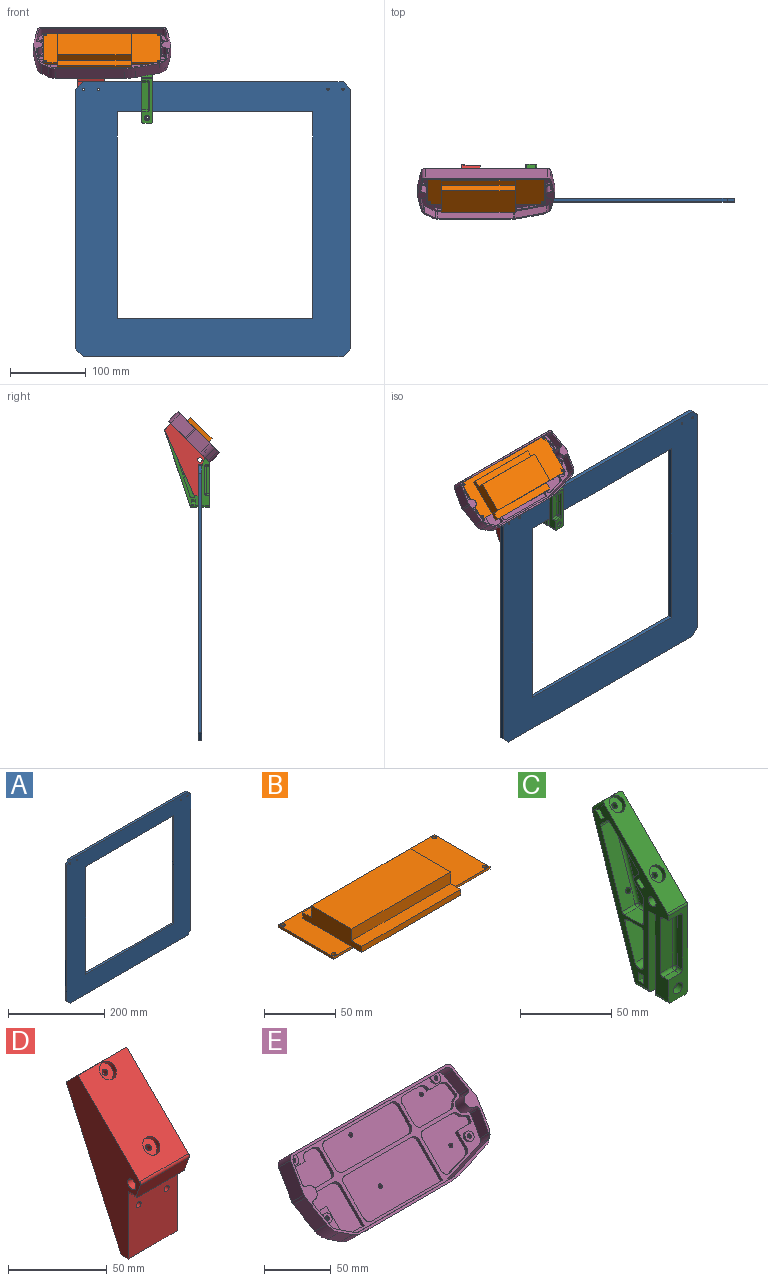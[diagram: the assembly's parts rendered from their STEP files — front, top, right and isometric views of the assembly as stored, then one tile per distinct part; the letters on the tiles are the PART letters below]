
ASSEMBLY  parts=5 mates=4
PART A: 18 faces, bbox 364x5x364 mm
  f0: plane 344x5mm, normal (-1,0,0), area 1720mm2, adj f12,f13,f16,f17
  f1: plane 344x5mm, normal (0,0,-1), area 1720mm2, adj f12,f13,f15,f16
  f2: plane 344x5mm, normal (1,0,0), area 1720mm2, adj f12,f13,f14,f15
  f3: plane 259x5mm, normal (0,0,1), area 1295mm2, adj f4,f6,f12,f13
  f4: plane 274x5mm, normal (1,0,0), area 1370mm2, adj f3,f5,f12,f13
  f5: plane 259x5mm, normal (0,0,-1), area 1295mm2, adj f4,f6,f12,f13
  f6: plane 274x5mm, normal (-1,0,0), area 1370mm2, adj f3,f5,f12,f13
  f7: cylinder r=1.5mm len=5mm, axis (0,1,0), area 47.1mm2, adj f12,f13
  f8: cylinder r=1.5mm len=5mm, axis (0,1,0), area 47.1mm2, adj f12,f13
  f9: cylinder r=1.5mm len=5mm, axis (0,1,0), area 47.1mm2, adj f12,f13
  f10: cylinder r=1.5mm len=5mm, axis (0,1,0), area 47.1mm2, adj f12,f13
  f11: plane 344x5mm, normal (0,0,1), area 1720mm2, adj f12,f13,f14,f17
  f12: plane 364x364mm, normal (0,-1,0), area 61301.7mm2, adj f0,f1,f2,f3,f4,f5,f6,f7
  f13: plane 364x364mm, normal (0,1,0), area 61301.7mm2, adj f0,f1,f2,f3,f4,f5,f6,f7
  f14: plane 10x10mm, normal (0.71,0,0.71), area 70.7mm2, adj f2,f11,f12,f13
  f15: plane 10x10mm, normal (0.71,0,-0.71), area 70.7mm2, adj f1,f2,f12,f13
  f16: plane 10x10mm, normal (-0.71,0,-0.71), area 70.7mm2, adj f0,f1,f12,f13
  f17: plane 10x10mm, normal (-0.71,0,0.71), area 70.7mm2, adj f0,f11,f12,f13
PART B: 20 faces, bbox 155x65x17 mm
  f0: plane 98x8.51mm, normal (0,0,1), area 834.2mm2, adj f12,f13,f15,f17
  f1: plane 155x55mm, normal (0,0,1), area 3732.3mm2, adj f2,f3,f4,f5,f6,f7,f8,f9
  f2: plane 155x2mm, normal (0,1,0), area 310mm2, adj f1,f3,f9,f10
  f3: plane 55x2mm, normal (-1,0,0), area 110mm2, adj f1,f2,f4,f10
  f4: plane 155x2mm, normal (0,-1,0), area 310mm2, adj f1,f3,f9,f10,f11
  f5: cylinder r=1.75mm len=3.5mm, axis (0,0,-1), area 22mm2, adj f1,f10
  f6: cylinder r=1.75mm len=3.5mm, axis (0,0,-1), area 22mm2, adj f1,f10
  f7: cylinder r=1.75mm len=3.5mm, axis (0,0,-1), area 22mm2, adj f1,f10
  f8: cylinder r=1.75mm len=3.5mm, axis (0,0,-1), area 22mm2, adj f1,f10
  f9: plane 55x2mm, normal (1,0,0), area 110mm2, adj f1,f2,f4,f10
  f10: plane 155x55mm, normal (0,0,-1), area 8486.5mm2, adj f2,f3,f4,f5,f6,f7,f8,f9
  f11: plane 98x10mm, normal (0,0,-1), area 980mm2, adj f4,f13,f14,f15
  f12: plane 98x5mm, normal (0,1,0), area 490mm2, adj f0,f1,f13,f15
  f13: plane 58.51x15mm, normal (-1,0,0), area 692.6mm2, adj f0,f1,f11,f12,f14,f16,f17,f18
  f14: plane 98x5mm, normal (0,-1,0), area 490mm2, adj f11,f13,f15,f16
  f15: plane 58.51x15mm, normal (1,0,0), area 692.6mm2, adj f0,f1,f11,f12,f14,f16,f17,f18
  f16: plane 98x10mm, normal (0,0,1), area 980mm2, adj f13,f14,f15,f18
  f17: plane 98x10mm, normal (0,1,0), area 980mm2, adj f0,f13,f15,f19
  f18: plane 98x10mm, normal (0,-1,0), area 980mm2, adj f13,f15,f16,f19
  f19: plane 98x40mm, normal (0,0,1), area 3920mm2, adj f13,f15,f17,f18
PART C: 98 faces, bbox 15.4x60.5x111.3 mm
  f0: cylinder r=1.75mm len=4mm, axis (0,-1,0), area 44mm2, adj f8,f79
  f1: cylinder r=1.7mm len=3.82mm, axis (0,-0.71,0.71), area 21.4mm2, adj f40,f50
  f2: cylinder r=1.7mm len=6.77mm, axis (0,-0.71,0.71), area 47.7mm2, adj f10,f58
  f3: plane 107.5x58.69mm, normal (-1,0,0), area 1499mm2, adj f5,f6,f7,f8,f10,f12,f25,f29
  f4: cylinder r=1.7mm len=6.35mm, axis (0,-0.71,0.71), area 50.6mm2, adj f10,f46
  f5: plane 59.17x15mm, normal (0,-1,0), area 409.1mm2, adj f3,f13,f14,f18,f25,f28,f31,f33
  f6: plane 55x15mm, normal (0,1,0), area 813.7mm2, adj f3,f7,f13,f14,f16,f28,f31
  f7: plane 15x5mm, normal (0,0,-1), area 75mm2, adj f3,f6,f8,f14
  f8: plane 55x15mm, normal (0,-1,0), area 813.7mm2, adj f0,f3,f7,f9,f14,f27,f30
  f9: plane 11x10mm, normal (0,0,-1), area 110mm2, adj f8,f10,f27,f30
  f10: plane 102.78x34.75mm, normal (0,0.95,-0.32), area 1586.6mm2, adj f2,f3,f4,f9,f11,f14,f15,f26
  f11: plane 11x8.49mm, normal (0,0.71,0.71), area 132mm2, adj f10,f12,f26,f29
  f12: plane 50.33x50.33mm, normal (0,-0.71,0.71), area 908.8mm2, adj f3,f11,f14,f19,f21,f25,f26,f29
  f13: plane 11x10mm, normal (0,0,-1), area 110mm2, adj f5,f6,f28,f31
  f14: plane 107.5x58.69mm, normal (1,0,0), area 3125.2mm2, adj f5,f6,f7,f8,f10,f12,f25,f26
  f15: cylinder r=1.75mm len=4.95mm, axis (0,-1,0), area 47.8mm2, adj f10,f77
  f16: cylinder r=1.75mm len=6mm, axis (0,-1,0), area 66mm2, adj f6,f17
  f17: plane 7x7mm, normal (0,-1,0), area 28.9mm2, adj f16,f18
  f18: cylinder r=3.5mm len=7mm, axis (0,-1,0), area 88mm2, adj f5,f17
  f19: cylinder r=5mm len=10mm, axis (0,-0.71,0.71), area 94.2mm2, adj f12,f20
  f20: plane 10x7.07mm, normal (0,-0.71,0.71), area 69.5mm2, adj f19,f24
  f21: cylinder r=5mm len=10mm, axis (0,-0.71,0.71), area 94.2mm2, adj f12,f22
  f22: plane 10x7.07mm, normal (0,-0.71,0.71), area 69.5mm2, adj f21,f23
  f23: cylinder r=1.7mm len=4.88mm, axis (0,-0.71,0.71), area 37.4mm2, adj f22,f47
  f24: cylinder r=1.7mm len=4.88mm, axis (0,-0.71,0.71), area 37.4mm2, adj f20,f41
  f25: cylinder r=2mm len=15mm, axis (1,0,0), area 23.6mm2, adj f3,f5,f12,f14
  f26: cylinder r=2mm len=10.6mm, axis (0,-0.71,0.71), area 38.8mm2, adj f10,f11,f12,f14
  f27: cylinder r=2mm len=10.67mm, axis (0,1,0), area 32.5mm2, adj f8,f9,f10,f14
  f28: cylinder r=2mm len=10mm, axis (0,1,0), area 31.4mm2, adj f5,f6,f13,f14
  f29: cylinder r=2mm len=10.6mm, axis (0,0.71,-0.71), area 38.8mm2, adj f3,f10,f11,f12
  f30: cylinder r=2mm len=10.67mm, axis (0,-1,0), area 32.5mm2, adj f3,f8,f9,f10
  f31: cylinder r=2mm len=10mm, axis (0,-1,0), area 31.4mm2, adj f3,f5,f6,f13
  f32: plane 36x9mm, normal (0,-1,0), area 324mm2, adj f3,f70,f73,f76
  f33: plane 9x4mm, normal (0,0,1), area 36mm2, adj f3,f5,f74,f76
  f34: plane 36x4mm, normal (-1,0,0), area 144mm2, adj f5,f71,f73,f74
  f35: plane 9x4mm, normal (0,0,-1), area 36mm2, adj f3,f5,f70,f71
  f36: plane 9.38x2.48mm, normal (0,0.71,0.71), area 32.8mm2, adj f3,f37,f40,f41
  f37: plane 4.45x4.45mm, normal (-0.87,0.35,0.35), area 11.3mm2, adj f36,f38,f40,f41
  f38: plane 4.45x4.45mm, normal (-0.87,-0.35,-0.35), area 11.3mm2, adj f37,f39,f40,f41
  f39: plane 9.38x2.48mm, normal (0,-0.71,-0.71), area 32.8mm2, adj f3,f38,f40,f41
  f40: plane 11x3.96mm, normal (0,-0.71,0.71), area 48mm2, adj f1,f3,f36,f37,f38,f39
  f41: plane 11x3.96mm, normal (0,0.71,-0.71), area 48mm2, adj f3,f24,f36,f37,f38,f39
  f42: plane 9.38x2.48mm, normal (0,0.71,0.71), area 32.8mm2, adj f3,f43,f46,f47
  f43: plane 4.45x4.45mm, normal (-0.87,0.35,0.35), area 11.3mm2, adj f42,f44,f46,f47
  f44: plane 4.45x4.45mm, normal (-0.87,-0.35,-0.35), area 11.3mm2, adj f43,f45,f46,f47
  f45: plane 9.38x2.48mm, normal (0,-0.71,-0.71), area 32.8mm2, adj f3,f44,f46,f47
  f46: plane 11x3.96mm, normal (0,-0.71,0.71), area 48mm2, adj f3,f4,f42,f43,f44,f45
  f47: plane 11x3.96mm, normal (0,0.71,-0.71), area 48mm2, adj f3,f23,f42,f43,f44,f45
  f48: plane 52.97x29.29mm, normal (-1,0,0), area 741.1mm2, adj f84,f87,f88,f90,f91,f92,f95,f96
  f49: cylinder r=2mm len=10mm, axis (-1,0,0), area 15.7mm2, adj f3,f50,f60,f94
  f50: plane 10x6.79mm, normal (0,0.71,-0.71), area 86.9mm2, adj f1,f3,f49,f51,f92
  f51: cylinder r=2mm len=10mm, axis (-1,0,0), area 31.4mm2, adj f3,f50,f52,f90
  f52: plane 10x2.83mm, normal (0,0.71,0.71), area 40mm2, adj f3,f51,f53,f88
  f53: cylinder r=2mm len=10mm, axis (-1,0,0), area 31.4mm2, adj f3,f52,f54,f86
  f54: plane 21.5x21.5mm, normal (0,0.71,-0.71), area 304mm2, adj f3,f53,f55,f84
  f55: cylinder r=2mm len=10mm, axis (-1,0,0), area 31.4mm2, adj f3,f54,f56,f85
  f56: plane 10x3.83mm, normal (0,-0.71,-0.71), area 54.1mm2, adj f3,f55,f57,f87
  f57: cylinder r=2mm len=10mm, axis (-1,0,0), area 22.2mm2, adj f3,f56,f58,f89
  f58: plane 49.14x16.5mm, normal (0,-0.95,0.32), area 508.3mm2, adj f2,f3,f57,f59,f91
  f59: cylinder r=2mm len=10mm, axis (-1,0,0), area 24.9mm2, adj f3,f58,f61,f93
  f60: plane 16.2x10mm, normal (0,1,0), area 162mm2, adj f3,f49,f62,f96
  f61: plane 12.78x10mm, normal (0,0,1), area 127.8mm2, adj f3,f59,f62,f95
  f62: cylinder r=2mm len=10mm, axis (-1,0,0), area 31.4mm2, adj f3,f60,f61,f97
  f63: plane 28.39x14.77mm, normal (-1,0,0), area 299.6mm2, adj f64,f65,f66,f67,f68,f69
  f64: cylinder r=2mm len=12mm, axis (-1,0,0), area 37.7mm2, adj f3,f63,f65,f69
  f65: plane 12x10.77mm, normal (0,0,-1), area 129.2mm2, adj f3,f63,f64,f66
  f66: cylinder r=2mm len=12mm, axis (-1,0,0), area 45.5mm2, adj f3,f63,f65,f67
  f67: plane 23.36x12mm, normal (0,-0.95,0.32), area 295.7mm2, adj f3,f63,f66,f68
  f68: cylinder r=3.5mm len=12mm, axis (-1,0,0), area 118.3mm2, adj f3,f63,f67,f69
  f69: plane 22.89x12mm, normal (0,1,0), area 274.6mm2, adj f3,f63,f64,f68
  f70: cylinder r=2mm len=9mm, axis (1,0,0), area 28.3mm2, adj f3,f32,f35,f72
  f71: cylinder r=2mm len=4mm, axis (0,1,0), area 12.6mm2, adj f5,f34,f35,f72
  f72: sphere r=2mm, area 6.3mm2, adj f70,f71,f73
  f73: cylinder r=2mm len=36mm, axis (0,0,-1), area 113.1mm2, adj f32,f34,f72,f75
  f74: cylinder r=2mm len=4mm, axis (0,-1,0), area 12.6mm2, adj f5,f33,f34,f75
  f75: sphere r=2mm, area 6.3mm2, adj f73,f74,f76
  f76: cylinder r=2mm len=9mm, axis (-1,0,0), area 28.3mm2, adj f3,f32,f33,f75
  f77: plane 13.8x5.6mm, normal (0,-1,0), area 63.1mm2, adj f3,f15,f78,f80,f81,f82
  f78: plane 12.18x4mm, normal (0,0,1), area 48.7mm2, adj f3,f77,f79,f82
  f79: plane 13.8x5.6mm, normal (0,1,0), area 63.1mm2, adj f0,f3,f78,f80,f81,f82
  f80: plane 12.18x4mm, normal (0,0,-1), area 48.7mm2, adj f3,f77,f79,f81
  f81: plane 4x2.8mm, normal (-0.87,0,-0.5), area 12.9mm2, adj f77,f79,f80,f82
  f82: plane 4x2.8mm, normal (-0.87,0,0.5), area 12.9mm2, adj f77,f78,f79,f81
  f83: cylinder r=3mm len=15mm, axis (1,0,0), area 282.7mm2, adj f3,f14
  f84: cylinder r=2mm len=22.91mm, axis (0,-0.71,-0.71), area 95.5mm2, adj f48,f54,f85,f86
  f85: sphere r=2mm, area 6.3mm2, adj f55,f84,f87
  f86: sphere r=2mm, area 6.3mm2, adj f53,f84,f88
  f87: cylinder r=2mm len=5.24mm, axis (0,-0.71,0.71), area 17mm2, adj f48,f56,f85,f89
  f88: cylinder r=2mm len=4.24mm, axis (0,0.71,-0.71), area 12.6mm2, adj f48,f52,f86,f90
  f89: sphere r=2mm, area 4.4mm2, adj f57,f87,f91
  f90: torus R=4mm, axis (1,0,0), area 13.5mm2, adj f48,f51,f88,f92
  f91: cylinder r=2mm len=49.78mm, axis (0,0.32,0.95), area 162.9mm2, adj f48,f58,f89,f93
  f92: cylinder r=2mm len=8.2mm, axis (0,-0.71,-0.71), area 30.2mm2, adj f48,f50,f90,f94
  f93: sphere r=2mm, area 5mm2, adj f59,f91,f95
  f94: sphere r=2mm, area 3.1mm2, adj f49,f92,f96
  f95: cylinder r=2mm len=12.78mm, axis (0,1,0), area 40.2mm2, adj f48,f61,f93,f97
  f96: cylinder r=2mm len=16.2mm, axis (0,0,-1), area 50.9mm2, adj f48,f60,f94,f97
  f97: sphere r=2mm, area 6.3mm2, adj f62,f95,f96
PART D: 81 faces, bbox 35.1x53.1x96 mm
  f0: plane 38.53x30.5mm, normal (0,1,0), area 395mm2, adj f2,f7,f8,f10,f11,f41,f46,f48
  f1: plane 31.13x31.13mm, normal (0,0.71,-0.71), area 409mm2, adj f2,f3,f4,f9,f42,f43,f44,f54
  f2: cylinder r=20mm len=20.5mm, axis (1,0,0), area 182.7mm2, adj f0,f1,f3,f12,f39,f41,f55,f71
  f3: plane 13.19x11.62mm, normal (1,0,0), area 58.5mm2, adj f1,f2,f5,f26,f29,f30,f39,f42
  f4: plane 16.35x14.35mm, normal (1,0,0), area 84.7mm2, adj f1,f6,f15,f31,f34,f35,f38,f43
  f5: plane 9.38x2.48mm, normal (0,-0.71,-0.71), area 32.8mm2, adj f3,f27,f29,f30
  f6: plane 9.38x2.48mm, normal (0,-0.71,-0.71), area 32.8mm2, adj f4,f32,f34,f35
  f7: plane 86.23x38.89mm, normal (0,0.91,-0.41), area 312.6mm2, adj f0,f8,f14,f19,f36,f51,f54,f56
  f8: plane 95.91x46.72mm, normal (1,0,0), area 436mm2, adj f0,f7,f13,f14,f15,f16,f17,f18
  f9: cylinder r=1.7mm len=3.82mm, axis (0,-0.71,0.71), area 21.4mm2, adj f1,f34
  f10: cylinder r=1.75mm len=6mm, axis (0,-1,0), area 66mm2, adj f0,f13
  f11: cylinder r=1.75mm len=6mm, axis (0,-1,0), area 66mm2, adj f0,f13
  f12: cylinder r=1.7mm len=4.3mm, axis (0,-0.71,0.71), area 25mm2, adj f2,f29
  f13: plane 42x35mm, normal (0,-1,0), area 1381.6mm2, adj f8,f10,f11,f14,f18,f19,f79
  f14: plane 35x5mm, normal (0,0,-1), area 175mm2, adj f7,f8,f13,f19
  f15: plane 35x7.51mm, normal (0,0.71,0.71), area 281.9mm2, adj f4,f8,f16,f19,f38,f75,f76,f77
  f16: plane 44.01x44.01mm, normal (0,-0.71,0.71), area 2021.5mm2, adj f8,f15,f19,f20,f22,f78
  f17: plane 35x9.8mm, normal (0,-0.94,-0.34), area 364.1mm2, adj f8,f18,f19,f78,f79
  f18: plane 33x5mm, normal (0,0,-1), area 165mm2, adj f8,f13,f17,f79
  f19: plane 95.91x52.69mm, normal (-1,0,0), area 1933.1mm2, adj f7,f13,f14,f15,f16,f17,f75,f78
  f20: cylinder r=5mm len=10mm, axis (0,-0.71,0.71), area 94.2mm2, adj f16,f21
  f21: plane 10x7.07mm, normal (0,-0.71,0.71), area 69.5mm2, adj f20,f25
  f22: cylinder r=5mm len=10mm, axis (0,-0.71,0.71), area 94.2mm2, adj f16,f23
  f23: plane 10x7.07mm, normal (0,-0.71,0.71), area 69.5mm2, adj f22,f24
  f24: cylinder r=1.7mm len=4.88mm, axis (0,-0.71,0.71), area 37.4mm2, adj f23,f35
  f25: cylinder r=1.7mm len=4.88mm, axis (0,-0.71,0.71), area 37.4mm2, adj f21,f30
  f26: plane 9.38x2.48mm, normal (0,0.71,0.71), area 32.8mm2, adj f3,f28,f29,f30
  f27: plane 4.45x4.45mm, normal (0.87,-0.35,-0.35), area 11.3mm2, adj f5,f28,f29,f30
  f28: plane 4.45x4.45mm, normal (0.87,0.35,0.35), area 11.3mm2, adj f26,f27,f29,f30
  f29: plane 11x3.96mm, normal (0,-0.71,0.71), area 48mm2, adj f3,f5,f12,f26,f27,f28
  f30: plane 11x3.96mm, normal (0,0.71,-0.71), area 48mm2, adj f3,f5,f25,f26,f27,f28
  f31: plane 9.38x2.48mm, normal (0,0.71,0.71), area 32.8mm2, adj f4,f33,f34,f35
  f32: plane 4.45x4.45mm, normal (0.87,-0.35,-0.35), area 11.3mm2, adj f6,f33,f34,f35
  f33: plane 4.45x4.45mm, normal (0.87,0.35,0.35), area 11.3mm2, adj f31,f32,f34,f35
  f34: plane 11x3.96mm, normal (0,-0.71,0.71), area 48mm2, adj f4,f6,f9,f31,f32,f33
  f35: plane 11x3.96mm, normal (0,0.71,-0.71), area 48mm2, adj f4,f6,f24,f31,f32,f33
  f36: plane 75.62x34.08mm, normal (1,0,0), area 700.9mm2, adj f7,f54,f55,f56
  f37: plane 8x1.36mm, normal (0,0.71,0.71), area 15.4mm2, adj f8,f53,f57,f60
  f38: plane 36.98x36.98mm, normal (0,0.71,-0.71), area 815mm2, adj f4,f8,f15,f49,f50,f53,f58,f68
  f39: plane 13x0.88mm, normal (0,0,-1), area 11.4mm2, adj f2,f3,f47,f71
  f40: plane 23x10.5mm, normal (0,1,0), area 194mm2, adj f8,f47,f48,f57,f62,f73
  f41: plane 11.06x2.07mm, normal (1,0,0), area 12mm2, adj f0,f2,f71,f72,f73,f74
  f42: plane 13x3.54mm, normal (0,0.71,0.71), area 65mm2, adj f1,f3,f50,f66
  f43: plane 13x3.54mm, normal (0,-0.71,-0.71), area 65mm2, adj f1,f4,f49,f70
  f44: plane 24.2x24.2mm, normal (1,0,0), area 197.1mm2, adj f1,f66,f67,f68,f69,f70
  f45: plane 23x16.28mm, normal (0,1,0), area 374.5mm2, adj f8,f51,f52,f64
  f46: plane 19.75x1mm, normal (1,0,0), area 18.7mm2, adj f0,f63,f64,f65
  f47: cylinder r=4mm len=15mm, axis (1,0,0), area 84.9mm2, adj f3,f39,f40,f61,f62,f72
  f48: cylinder r=4mm len=23mm, axis (1,0,0), area 121.3mm2, adj f0,f8,f40,f74
  f49: cylinder r=4mm len=13mm, axis (-1,0,0), area 81.7mm2, adj f4,f38,f43,f69
  f50: cylinder r=4mm len=15mm, axis (-1,0,0), area 84.9mm2, adj f3,f38,f42,f58,f67
  f51: cylinder r=4mm len=23mm, axis (1,0,0), area 118.9mm2, adj f7,f8,f45,f65
  f52: cylinder r=4mm len=23mm, axis (1,0,0), area 121.3mm2, adj f0,f8,f45,f63
  f53: cylinder r=4mm len=8mm, axis (-1,0,0), area 50.3mm2, adj f8,f37,f38,f59
  f54: cylinder r=2mm len=32.54mm, axis (0,0.71,0.71), area 136.2mm2, adj f1,f7,f36,f55,f77
  f55: torus R=18mm, axis (1,0,0), area 47.6mm2, adj f2,f36,f54,f56
  f56: cylinder r=2mm len=38.53mm, axis (0,0,1), area 116mm2, adj f0,f7,f36,f55
  f57: cylinder r=2mm len=8mm, axis (1,0,0), area 12.6mm2, adj f8,f37,f40,f61
  f58: cylinder r=2mm len=10.32mm, axis (0,-0.71,-0.71), area 33.4mm2, adj f3,f38,f50,f59
  f59: torus R=2mm, axis (1,0,0), area 16.2mm2, adj f3,f53,f58,f60
  f60: cylinder r=2mm len=2.78mm, axis (0,0.71,-0.71), area 6.1mm2, adj f3,f37,f59,f61
  f61: torus R=4mm, axis (1,0,0), area 6.7mm2, adj f3,f47,f57,f60,f62
  f62: cylinder r=2mm len=3.17mm, axis (0,0,1), area 3.9mm2, adj f40,f47,f61
  f63: torus R=2mm, axis (1,0,0), area 13mm2, adj f0,f46,f52,f64
  f64: cylinder r=2mm len=16.28mm, axis (0,0,-1), area 51.1mm2, adj f45,f46,f63,f65
  f65: torus R=2mm, axis (1,0,0), area 12.9mm2, adj f0,f7,f46,f51,f64
  f66: cylinder r=2mm len=4.95mm, axis (0,0.71,-0.71), area 15.7mm2, adj f1,f42,f44,f67
  f67: torus R=2mm, axis (1,0,0), area 16.2mm2, adj f44,f50,f66,f68
  f68: cylinder r=2mm len=18.67mm, axis (0,-0.71,-0.71), area 76.7mm2, adj f38,f44,f67,f69
  f69: torus R=2mm, axis (1,0,0), area 16.2mm2, adj f44,f49,f68,f70
  f70: cylinder r=2mm len=4.95mm, axis (0,-0.71,0.71), area 15.7mm2, adj f1,f43,f44,f69
  f71: cylinder r=2mm len=2mm, axis (0,-1,0), area 1.8mm2, adj f2,f39,f41,f72
  f72: torus R=2mm, axis (1,0,0), area 16.2mm2, adj f41,f47,f71,f73
  f73: cylinder r=2mm len=7.33mm, axis (0,0,-1), area 23mm2, adj f40,f41,f72,f74
  f74: torus R=2mm, axis (1,0,0), area 13mm2, adj f0,f41,f48,f73
  f75: cylinder r=2mm len=3mm, axis (1,0,0), area 6.5mm2, adj f7,f15,f19,f77
  f76: cylinder r=2mm len=20.5mm, axis (1,0,0), area 64.4mm2, adj f1,f4,f15,f77
  f77: torus R=4mm, axis (0,0.71,0.71), area 5.9mm2, adj f7,f15,f54,f75,f76
  f78: cylinder r=2mm len=35mm, axis (-1,0,0), area 79.4mm2, adj f8,f16,f17,f19
  f79: cylinder r=2mm len=5.73mm, axis (0,-1,0), area 16.5mm2, adj f13,f17,f18,f19
  f80: cylinder r=3mm len=35mm, axis (1,0,0), area 659.7mm2, adj f8,f19
PART E: 169 faces, bbox 182x67.5x67.5 mm
  f0: plane 8x5.66mm, normal (0,-0.71,0.71), area 41.2mm2, adj f27,f138
  f1: plane 8x5.66mm, normal (0,-0.71,0.71), area 41.2mm2, adj f26,f137
  f2: plane 8x4.95mm, normal (0,-0.71,0.71), area 40.1mm2, adj f25,f79,f132,f133,f134
  f3: plane 8x4.95mm, normal (0,-0.71,0.71), area 40.1mm2, adj f24,f79,f131,f135,f136
  f4: cylinder r=5mm len=5.66mm, axis (0,-0.71,0.71), area 23.6mm2, adj f101,f104,f105,f139
  f5: cylinder r=5mm len=5.66mm, axis (0,0.71,-0.71), area 23.6mm2, adj f103,f104,f105,f139
  f6: cylinder r=5mm len=5.66mm, axis (0,0.71,-0.71), area 23.6mm2, adj f101,f102,f105,f139
  f7: cylinder r=5mm len=4.33mm, axis (0,-0.71,0.71), area 15.7mm2, adj f106,f115,f116,f139
  f8: cylinder r=5mm len=6.26mm, axis (0,0.71,-0.71), area 27.4mm2, adj f107,f108,f116,f139
  f9: cylinder r=5mm len=5.66mm, axis (0,0.71,-0.71), area 23.6mm2, adj f106,f107,f116,f139
  f10: cylinder r=5mm len=5.66mm, axis (0,0.71,-0.71), area 23.6mm2, adj f117,f124,f125,f139
  f11: cylinder r=5mm len=5mm, axis (0,0.71,-0.71), area 20.8mm2, adj f122,f123,f125,f139
  f12: cylinder r=5mm len=4.33mm, axis (0,-0.71,0.71), area 15.7mm2, adj f119,f120,f125,f139
  f13: cylinder r=5mm len=5.66mm, axis (0,0.71,-0.71), area 23.6mm2, adj f118,f119,f125,f139
  f14: cylinder r=5mm len=5.66mm, axis (0,0.71,-0.71), area 23.6mm2, adj f117,f118,f125,f139
  f15: cylinder r=5mm len=5.66mm, axis (0,0.71,-0.71), area 23.6mm2, adj f126,f129,f130,f139
  f16: cylinder r=5mm len=5.66mm, axis (0,0.71,-0.71), area 23.6mm2, adj f128,f129,f130,f139
  f17: cylinder r=5mm len=5.66mm, axis (0,-0.71,0.71), area 23.6mm2, adj f127,f128,f130,f139
  f18: cylinder r=5mm len=5.66mm, axis (0,-0.71,0.71), area 23.6mm2, adj f126,f127,f130,f139
  f19: cylinder r=1.7mm len=5.59mm, axis (0,-0.71,0.71), area 48.1mm2, adj f94,f130
  f20: cylinder r=1.7mm len=5.59mm, axis (0,-0.71,0.71), area 48.1mm2, adj f100,f125
  f21: cylinder r=1.7mm len=5.59mm, axis (0,-0.71,0.71), area 48.1mm2, adj f98,f116
  f22: cylinder r=1.7mm len=5.59mm, axis (0,-0.71,0.71), area 48.1mm2, adj f96,f105
  f23: plane 182x54.8mm, normal (0,-0.71,0.71), area 1121.2mm2, adj f29,f30,f31,f32,f33,f34,f35,f36
  f24: cylinder r=1.7mm len=4.53mm, axis (0,0.71,-0.71), area 32mm2, adj f3,f51
  f25: cylinder r=1.7mm len=4.53mm, axis (0,0.71,-0.71), area 32mm2, adj f2,f72
  f26: cylinder r=1.7mm len=4.53mm, axis (0,0.71,-0.71), area 32mm2, adj f1,f65
  f27: cylinder r=1.7mm len=4.53mm, axis (0,0.71,-0.71), area 32mm2, adj f0,f58
  f28: plane 182x54.8mm, normal (0,0.71,-0.71), area 12526.3mm2, adj f29,f30,f31,f32,f33,f34,f35,f36
  f29: plane 91.62x12.73mm, normal (0,-0.71,-0.71), area 1649.1mm2, adj f23,f28,f41,f42
  f30: plane 31.36x18.5mm, normal (0.25,-0.68,-0.68), area 583.3mm2, adj f23,f28,f39,f42
  f31: plane 28.31x28.31mm, normal (0.98,-0.13,-0.13), area 403.7mm2, adj f23,f28,f32,f39
  f32: cylinder r=6mm len=14.29mm, axis (0,0.71,-0.71), area 40.1mm2, adj f23,f28,f31,f33
  f33: plane 32.04x32.04mm, normal (0.98,0.13,0.13), area 500.3mm2, adj f23,f28,f32,f43
  f34: plane 161.7x12.73mm, normal (0,0.71,0.71), area 2910.7mm2, adj f23,f28,f43,f44
  f35: plane 32.04x32.04mm, normal (-0.98,0.13,0.13), area 500.3mm2, adj f23,f28,f36,f44
  f36: cylinder r=6mm len=14.29mm, axis (0,0.71,-0.71), area 40.1mm2, adj f23,f28,f35,f37
  f37: plane 30.65x30.65mm, normal (-0.98,-0.13,-0.13), area 464.3mm2, adj f23,f28,f36,f40
  f38: plane 17.19x17.19mm, normal (-0.57,-0.58,-0.58), area 199.2mm2, adj f23,f28,f40,f41
  f39: cylinder r=15mm len=21.03mm, axis (0,-0.71,0.71), area 305.2mm2, adj f23,f28,f30,f31
  f40: cylinder r=15mm len=19.48mm, axis (0,-0.71,0.71), area 210.1mm2, adj f23,f28,f37,f38
  f41: cylinder r=15mm len=14.62mm, axis (0,0.71,-0.71), area 163.9mm2, adj f23,f28,f29,f38
  f42: cylinder r=60mm len=15.12mm, axis (0,0.71,-0.71), area 275.1mm2, adj f23,f28,f29,f30
  f43: cylinder r=5mm len=15.61mm, axis (0,0.71,-0.71), area 124.7mm2, adj f23,f28,f33,f34
  f44: cylinder r=5mm len=15.61mm, axis (0,0.71,-0.71), area 124.7mm2, adj f23,f28,f34,f35
  f45: plane 10x2.83mm, normal (0,0.71,0.71), area 40mm2, adj f28,f46,f50,f51
  f46: plane 4.99x4.99mm, normal (0.87,0.35,0.35), area 14.1mm2, adj f28,f45,f47,f51
  f47: plane 4.99x4.99mm, normal (0.87,-0.35,-0.35), area 14.1mm2, adj f28,f46,f48,f51
  f48: plane 10x2.83mm, normal (0,-0.71,-0.71), area 40mm2, adj f28,f47,f49,f51
  f49: plane 4.99x4.99mm, normal (-0.87,-0.35,-0.35), area 14.1mm2, adj f28,f48,f50,f51
  f50: plane 4.99x4.99mm, normal (-0.87,0.35,0.35), area 14.1mm2, adj f28,f45,f49,f51
  f51: plane 13.52x4.31mm, normal (0,0.71,-0.71), area 62.7mm2, adj f24,f45,f46,f47,f48,f49,f50
  f52: plane 4.07x4.07mm, normal (-0.5,-0.61,-0.61), area 14.1mm2, adj f28,f53,f57,f58
  f53: plane 9.9x9.9mm, normal (-1,0,0), area 40mm2, adj f28,f52,f54,f58
  f54: plane 4.07x4.07mm, normal (-0.5,0.61,0.61), area 14.1mm2, adj f28,f53,f55,f58
  f55: plane 4.07x4.07mm, normal (0.5,0.61,0.61), area 14.1mm2, adj f28,f54,f56,f58
  f56: plane 9.9x9.9mm, normal (1,0,0), area 40mm2, adj f28,f55,f57,f58
  f57: plane 4.07x4.07mm, normal (0.5,-0.61,-0.61), area 14.1mm2, adj f28,f52,f56,f58
  f58: plane 9.56x9.56mm, normal (0,0.71,-0.71), area 62.7mm2, adj f27,f52,f53,f54,f55,f56,f57
  f59: plane 4.07x4.07mm, normal (0.5,0.61,0.61), area 14.1mm2, adj f28,f60,f64,f65
  f60: plane 9.9x9.9mm, normal (1,0,0), area 40mm2, adj f28,f59,f61,f65
  f61: plane 4.07x4.07mm, normal (0.5,-0.61,-0.61), area 14.1mm2, adj f28,f60,f62,f65
  f62: plane 4.07x4.07mm, normal (-0.5,-0.61,-0.61), area 14.1mm2, adj f28,f61,f63,f65
  f63: plane 9.9x9.9mm, normal (-1,0,0), area 40mm2, adj f28,f62,f64,f65
  f64: plane 4.07x4.07mm, normal (-0.5,0.61,0.61), area 14.1mm2, adj f28,f59,f63,f65
  f65: plane 9.56x9.56mm, normal (0,0.71,-0.71), area 62.7mm2, adj f26,f59,f60,f61,f62,f63,f64
  f66: plane 4.99x4.99mm, normal (-0.87,0.35,0.35), area 14.1mm2, adj f28,f67,f71,f72
  f67: plane 10x2.83mm, normal (0,0.71,0.71), area 40mm2, adj f28,f66,f68,f72
  f68: plane 4.99x4.99mm, normal (0.87,0.35,0.35), area 14.1mm2, adj f28,f67,f69,f72
  f69: plane 4.99x4.99mm, normal (0.87,-0.35,-0.35), area 14.1mm2, adj f28,f68,f70,f72
  f70: plane 10x2.83mm, normal (0,-0.71,-0.71), area 40mm2, adj f28,f69,f71,f72
  f71: plane 4.99x4.99mm, normal (-0.87,-0.35,-0.35), area 14.1mm2, adj f28,f66,f70,f72
  f72: plane 13.52x4.31mm, normal (0,0.71,-0.71), area 62.7mm2, adj f25,f66,f67,f68,f69,f70,f71
  f73: plane 22.92x22.92mm, normal (-0.98,0.13,0.13), area 256.8mm2, adj f23,f74,f92,f139
  f74: cylinder r=2mm len=10.87mm, axis (0,-0.71,0.71), area 47.4mm2, adj f23,f73,f75,f139
  f75: cylinder r=6mm len=17.68mm, axis (0,-0.71,0.71), area 255.5mm2, adj f23,f74,f76,f139
  f76: cylinder r=2mm len=10.87mm, axis (0,-0.71,0.71), area 47.4mm2, adj f23,f75,f77,f139
  f77: plane 21.97x21.97mm, normal (-0.98,-0.13,-0.13), area 239mm2, adj f23,f76,f78,f139
  f78: cylinder r=5mm len=12.08mm, axis (0,-0.71,0.71), area 90mm2, adj f23,f77,f79,f139
  f79: plane 158.39x9.19mm, normal (0,-0.71,-0.71), area 2027mm2, adj f2,f3,f23,f78,f80,f131,f132,f134
  f80: cylinder r=5mm len=12.08mm, axis (0,-0.71,0.71), area 90mm2, adj f23,f79,f81,f139
  f81: plane 21.97x21.97mm, normal (0.98,-0.13,-0.13), area 239mm2, adj f23,f80,f82,f139
  f82: cylinder r=2mm len=10.87mm, axis (0,-0.71,0.71), area 47.4mm2, adj f23,f81,f83,f139
  f83: cylinder r=6mm len=17.68mm, axis (0,-0.71,0.71), area 255.5mm2, adj f23,f82,f84,f139
  f84: cylinder r=2mm len=10.87mm, axis (0,-0.71,0.71), area 47.4mm2, adj f23,f83,f85,f139
  f85: plane 24.01x24.01mm, normal (0.98,0.13,0.13), area 277.2mm2, adj f23,f84,f86,f139
  f86: cylinder r=5mm len=11.44mm, axis (0,-0.71,0.71), area 50.6mm2, adj f23,f85,f87,f139
  f87: plane 15.99x15.99mm, normal (0.57,0.58,0.58), area 219.1mm2, adj f23,f86,f88,f139
  f88: cylinder r=5mm len=9.82mm, axis (0,-0.71,0.71), area 39.5mm2, adj f23,f87,f89,f139
  f89: plane 100.91x9.19mm, normal (0,0.71,0.71), area 1311.8mm2, adj f23,f88,f90,f139
  f90: cylinder r=5mm len=9.31mm, axis (0,-0.71,0.71), area 16.6mm2, adj f23,f89,f91,f139
  f91: plane 42.84x17.08mm, normal (-0.25,0.68,0.68), area 575.4mm2, adj f23,f90,f92,f139
  f92: cylinder r=5mm len=11.96mm, axis (0,-0.71,0.71), area 73.5mm2, adj f23,f73,f91,f139
  f93: cylinder r=5mm len=10mm, axis (0,-0.71,0.71), area 78.5mm2, adj f28,f94
  f94: plane 10x7.07mm, normal (0,0.71,-0.71), area 69.5mm2, adj f19,f93
  f95: cylinder r=5mm len=10mm, axis (0,-0.71,0.71), area 78.5mm2, adj f28,f96
  f96: plane 10x7.07mm, normal (0,0.71,-0.71), area 69.5mm2, adj f22,f95
  f97: cylinder r=5mm len=10mm, axis (0,-0.71,0.71), area 78.5mm2, adj f28,f98
  f98: plane 10x7.07mm, normal (0,0.71,-0.71), area 69.5mm2, adj f21,f97
  f99: cylinder r=5mm len=10mm, axis (0,-0.71,0.71), area 78.5mm2, adj f28,f100
  f100: plane 10x7.07mm, normal (0,0.71,-0.71), area 69.5mm2, adj f20,f99
  f101: plane 22.98x22.98mm, normal (1,0,0), area 88.5mm2, adj f4,f6,f105,f139
  f102: plane 75x2.12mm, normal (0,0.71,0.71), area 225mm2, adj f6,f103,f105,f139
  f103: plane 26.52x26.52mm, normal (-1,0,0), area 103.5mm2, adj f5,f102,f105,f139
  f104: plane 70x2.12mm, normal (0,-0.71,-0.71), area 210mm2, adj f4,f5,f105,f139
  f105: plane 80x27.93mm, normal (0,-0.71,0.71), area 3134.8mm2, adj f4,f5,f6,f22,f101,f102,f103,f104
  f106: plane 30.74x2.12mm, normal (0,-0.71,-0.71), area 92.2mm2, adj f7,f9,f116,f139
  f107: plane 21.66x21.66mm, normal (1,0,0), area 82.9mm2, adj f8,f9,f116,f139
  f108: plane 21x5.99mm, normal (-0.25,0.68,0.68), area 65.1mm2, adj f8,f109,f116,f139
  f109: cylinder r=5mm len=5.54mm, axis (0,-0.71,0.71), area 19.7mm2, adj f108,f110,f116,f139
  f110: plane 12.14x12.14mm, normal (-1,0,0), area 42.5mm2, adj f109,f111,f116,f139
  f111: plane 13.65x2.12mm, normal (0,0.71,0.71), area 41mm2, adj f110,f112,f116,f139
  f112: cylinder r=2mm len=3.27mm, axis (0,-0.71,0.71), area 8.3mm2, adj f111,f113,f116,f139
  f113: plane 4.01x4.01mm, normal (-0.98,0.13,0.13), area 8.2mm2, adj f112,f114,f116,f139
  f114: cylinder r=2mm len=3.77mm, axis (0,-0.71,0.71), area 9.4mm2, adj f113,f115,f116,f139
  f115: cylinder r=8mm len=5.45mm, axis (0,-0.71,0.71), area 20.7mm2, adj f7,f114,f116,f139
  f116: plane 47.15x26.61mm, normal (0,-0.71,0.71), area 1226.1mm2, adj f7,f8,f9,f21,f106,f107,f108,f109
  f117: plane 17.3x2.12mm, normal (0,-0.71,-0.71), area 51.9mm2, adj f10,f14,f125,f139
  f118: plane 14.14x14.14mm, normal (1,0,0), area 51mm2, adj f13,f14,f125,f139
  f119: plane 30.74x2.12mm, normal (0,0.71,0.71), area 92.2mm2, adj f12,f13,f125,f139
  f120: cylinder r=8mm len=5.45mm, axis (0,-0.71,0.71), area 20.7mm2, adj f12,f121,f125,f139
  f121: cylinder r=2mm len=3.77mm, axis (0,-0.71,0.71), area 9.4mm2, adj f120,f122,f125,f139
  f122: plane 7.94x7.94mm, normal (-0.98,-0.13,-0.13), area 25.1mm2, adj f11,f121,f125,f139
  f123: plane 13.36x2.12mm, normal (0,-0.71,-0.71), area 40.1mm2, adj f11,f124,f125,f139
  f124: plane 2.83x2.83mm, normal (-1,0,0), area 3mm2, adj f10,f123,f125,f139
  f125: plane 47.15x19.09mm, normal (0,-0.71,0.71), area 1069mm2, adj f10,f11,f12,f13,f14,f20,f117,f118
  f126: plane 70x2.12mm, normal (0,-0.71,-0.71), area 210mm2, adj f15,f18,f130,f139
  f127: plane 14.14x14.14mm, normal (1,0,0), area 51mm2, adj f17,f18,f130,f139
  f128: plane 70x2.12mm, normal (0,0.71,0.71), area 210mm2, adj f16,f17,f130,f139
  f129: plane 14.14x14.14mm, normal (-1,0,0), area 51mm2, adj f15,f16,f130,f139
  f130: plane 80x19.09mm, normal (0,-0.71,0.71), area 2129.5mm2, adj f15,f16,f17,f18,f19,f126,f127,f128
  f131: plane 3.54x3.54mm, normal (-1,0,0), area 6mm2, adj f3,f79,f136,f139
  f132: plane 3.54x3.54mm, normal (1,0,0), area 6mm2, adj f2,f79,f133,f139
  f133: cylinder r=4mm len=8mm, axis (0,-0.71,0.71), area 25.1mm2, adj f2,f132,f134,f139
  f134: plane 3.54x3.54mm, normal (-1,0,0), area 6mm2, adj f2,f79,f133,f139
  f135: plane 3.54x3.54mm, normal (1,0,0), area 6mm2, adj f3,f79,f136,f139
  f136: cylinder r=4mm len=8mm, axis (0,-0.71,0.71), area 25.1mm2, adj f3,f131,f135,f139
  f137: cylinder r=4mm len=8mm, axis (0,-0.71,0.71), area 50.3mm2, adj f1,f139
  f138: cylinder r=4mm len=8mm, axis (0,-0.71,0.71), area 50.3mm2, adj f0,f139
  f139: plane 175.07x51.97mm, normal (0,-0.71,0.71), area 2424.7mm2, adj f4,f5,f6,f7,f8,f9,f10,f11
  f140: plane 37.15x19.09mm, normal (0,-0.71,0.71), area 808.1mm2, adj f141,f142,f143,f144,f145,f146,f147,f148
  f141: cylinder r=5mm len=5.66mm, axis (0,0.71,-0.71), area 23.6mm2, adj f139,f140,f152,f153
  f142: cylinder r=5mm len=5.66mm, axis (0,0.71,-0.71), area 23.6mm2, adj f139,f140,f151,f152
  f143: cylinder r=5mm len=4.33mm, axis (0,-0.71,0.71), area 15.7mm2, adj f139,f140,f145,f146
  f144: cylinder r=5mm len=5.66mm, axis (0,0.71,-0.71), area 23.6mm2, adj f139,f140,f145,f153
  f145: plane 20.74x2.12mm, normal (0,0.71,0.71), area 62.2mm2, adj f139,f140,f143,f144
  f146: cylinder r=8mm len=5.45mm, axis (0,-0.71,0.71), area 20.7mm2, adj f139,f140,f143,f147
  f147: cylinder r=2mm len=3.77mm, axis (0,-0.71,0.71), area 9.4mm2, adj f139,f140,f146,f149
  f148: cylinder r=5mm len=5mm, axis (0,-0.71,0.71), area 20.8mm2, adj f139,f140,f149,f150
  f149: plane 7.94x7.94mm, normal (0.98,-0.13,-0.13), area 25.1mm2, adj f139,f140,f147,f148
  f150: plane 13.36x2.12mm, normal (0,-0.71,-0.71), area 40.1mm2, adj f139,f140,f148,f151
  f151: plane 2.83x2.83mm, normal (1,0,0), area 3mm2, adj f139,f140,f142,f150
  f152: plane 7.3x2.12mm, normal (0,-0.71,-0.71), area 21.9mm2, adj f139,f140,f141,f142
  f153: plane 14.14x14.14mm, normal (-1,0,0), area 51mm2, adj f139,f140,f141,f144
  f154: plane 37.15x27.93mm, normal (0,-0.71,0.71), area 978.8mm2, adj f155,f156,f157,f158,f159,f160,f161,f162
  f155: cylinder r=5mm len=5.66mm, axis (0,0.71,-0.71), area 23.6mm2, adj f139,f154,f165,f166
  f156: plane 3.05x3.05mm, normal (0.57,0.58,0.58), area 6.9mm2, adj f139,f154,f157,f168
  f157: cylinder r=5mm len=5.03mm, axis (0,-0.71,0.71), area 14.5mm2, adj f139,f154,f156,f158
  f158: plane 16.39x16.39mm, normal (1,0,0), area 60.6mm2, adj f139,f154,f157,f159
  f159: plane 13.65x2.12mm, normal (0,0.71,0.71), area 41mm2, adj f139,f154,f158,f160
  f160: cylinder r=2mm len=3.27mm, axis (0,-0.71,0.71), area 8.3mm2, adj f139,f154,f159,f161
  f161: plane 4.01x4.01mm, normal (0.98,0.13,0.13), area 8.2mm2, adj f139,f154,f160,f162
  f162: cylinder r=2mm len=3.77mm, axis (0,-0.71,0.71), area 9.4mm2, adj f139,f154,f161,f164
  f163: cylinder r=5mm len=4.33mm, axis (0,-0.71,0.71), area 15.7mm2, adj f139,f154,f164,f165
  f164: cylinder r=8mm len=5.45mm, axis (0,-0.71,0.71), area 20.7mm2, adj f139,f154,f162,f163
  f165: plane 20.74x2.12mm, normal (0,-0.71,-0.71), area 62.2mm2, adj f139,f154,f155,f163
  f166: plane 26.52x26.52mm, normal (-1,0,0), area 103.5mm2, adj f139,f154,f155,f167
  f167: plane 14.11x2.12mm, normal (0,0.71,0.71), area 42.3mm2, adj f139,f154,f166,f168
  f168: cylinder r=5mm len=2.85mm, axis (0,-0.71,0.71), area 9.1mm2, adj f139,f154,f156,f167
PLACE A t=(-263.99,-146.35,18.22)mm
PLACE B rot(axis=(1,0,0),45deg) t=(-410.99,-133.42,243.05)mm
PLACE C t=(-263.99,-146.35,18.22)mm
PLACE D t=(-263.99,-146.35,18.22)mm
PLACE E t=(-263.99,-146.35,18.22)mm
MATE fastened D.f9 <-> E.f93  axis (0,-0.71,0.71) through (-425.99,-114.33,252.24)mm
MATE fastened D.f10 <-> A.f9  axis (0,-1,0) through (-415.99,-146.35,190.22)mm
MATE fastened E.f99 <-> C.f21  axis (0,0.71,-0.71) through (-351.49,-114.33,252.24)mm
MATE fastened B.f5 <-> E.f133  axis (0,0.71,-0.71) through (-485.99,-115.74,260.72)mm
